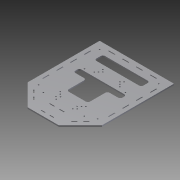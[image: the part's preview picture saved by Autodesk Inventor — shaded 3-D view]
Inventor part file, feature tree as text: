
AUTODESK INVENTOR PART (.ipt)
format: ipt  version: 2012 (Build 160160000, 160)  size: 351,232 bytes
history: native  units: mm
features: sketch x2, extrude x1, hole x1
ambient origin geometry x8: Origin, YZ Plane, XZ Plane, XY Plane, X Axis, Y Axis, Z Axis, Center Point
bodies: Solid1 (feature_tree)
feature tree (4):
  extrude  "Extrusion1"  Depth=3.0mm TaperAngle=0.0deg
  hole  "Hole1"  [1 undecoded]
  sketch  "Sketch1"  dims[d12=10.0mm d13=2.0mm d16=10.0mm d17=2.0mm d19=10.0mm d20=2.0mm d23=10.0mm d24=2.0mm d25=10.0mm d26=10.0mm d27=2.0mm d28=10.0mm d29=2.0mm d30=10.0mm d33=15.0mm d34=2.0mm d36=15.0mm d37=18.0mm d38=15.0mm d39=17.0mm d40=2.0mm d41=15.0mm d43=15.0mm d44=18.0mm d45=15.0mm d46=17.0mm d47=15.0mm d48=18.0mm d52=15.0mm d54=18.0mm d55=219.764931mm d56=174.51mm d112=2.0mm d113=12.0mm d114=12.0mm d116=11.0mm d208=50.0mm d211=60.0mm d212=5.0mm d213=110.0mm d214=20.0mm d217=5.0mm d254=30.0mm d255=30.0mm d256=5.0mm d257=3.0mm d258=0.0mm]
  sketch  "Sketch2"  dims[d259=10.0mm d260=2.0mm d261=10.0mm d262=2.0mm d263=10.0mm d264=2.0mm d265=10.0mm d266=2.0mm d267=10.0mm d268=10.0mm d269=2.0mm d270=10.0mm d271=2.0mm d272=10.0mm d273=15.0mm d274=2.0mm d275=15.0mm d276=18.0mm d277=15.0mm d278=17.0mm d279=2.0mm d280=15.0mm d281=15.0mm d282=18.0mm d283=15.0mm d284=17.0mm d285=15.0mm d286=18.0mm d287=15.0mm d288=18.0mm d289=219.764931mm d290=174.51mm d291=3.0mm d292=3.0mm d293=3.0mm d294=3.0mm d295=3.0mm d296=-5.117mm d297=10.0mm d298=15.117mm d299=10.0mm d300=5.554212mm d301=5.0mm d302=5.0mm d303=5.554212mm d304=5.554212mm d305=5.0mm d306=5.0mm d307=3.0mm d308=3.0mm d309=3.0mm d310=5.117mm d311=0.0mm d312=15.117007mm d313=3.0mm d314=5.0mm d315=5.0mm d316=5.0mm d317=5.000007mm d318=5.0mm d319=2.0mm d320=12.0mm d321=12.0mm d322=11.0mm d323=3.0mm d324=3.0mm d325=3.0mm d326=95.933639mm d327=95.933639mm d328=50.0mm d329=60.0mm d330=5.0mm d331=110.0mm d332=20.0mm d333=10.0mm d334=5.0mm d335=30.0mm d336=30.0mm d337=5.0mm d338=3.0mm d339=6.0mm d340=4.0mm d341=2.0mm d342=90.0deg d343=8.0mm d344=20.594885mm]
note: 1 required parameter value undecoded (feature->parameter linkage not recoverable at this tier; creation-order binding heuristic only, values carry confidence <= 0.55)
